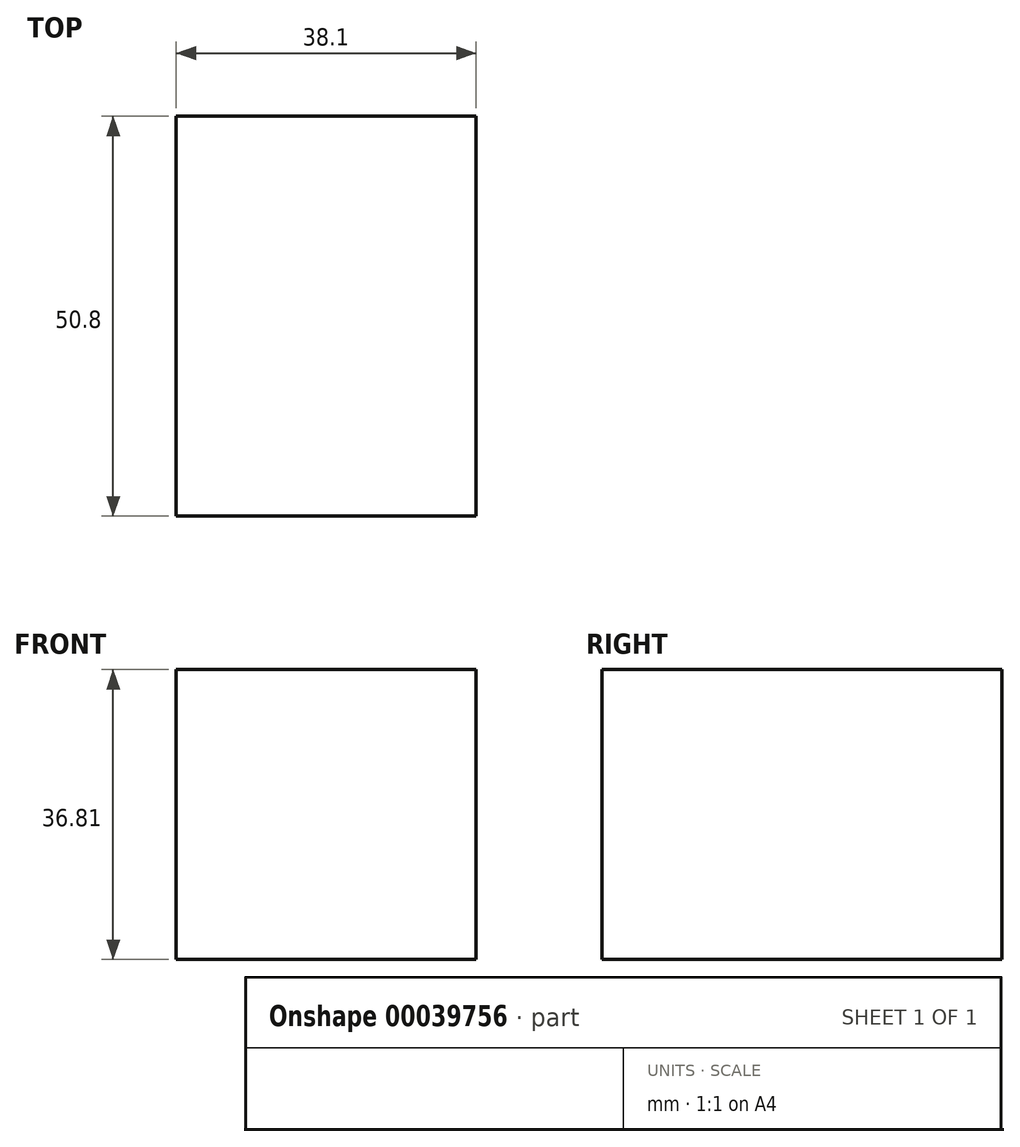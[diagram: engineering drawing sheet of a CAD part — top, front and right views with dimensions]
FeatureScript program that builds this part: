
annotation { "Feature Type Name" : "Feature", "Feature Type Description" : "" }
export const myFeature = defineFeature(function(context is Context, id is Id, definition is map)
    precondition{}
    {
        {
            var Q0;
            Q0=qCreatedBy(makeId("Front.planeOp"),FACE);
            var sketch = newSketch(context, id + "F0", { "sketchPlane" : qUnion([Q0])});
            skLineSegment(sketch, "E0.bottom", {"start": v(0, 0) * mm, "end": v(38.1, 0) * mm});
            skLineSegment(sketch, "E0.top", {"start": v(0, 36.8) * mm, "end": v(38.1, 36.8) * mm});
            skLineSegment(sketch, "E0.left", {"start": v(0, 0) * mm, "end": v(0, 36.8) * mm});
            skLineSegment(sketch, "E0.right", {"start": v(38.1, 0) * mm, "end": v(38.1, 36.8) * mm});
            skSolve(sketch);
        }
        {
            var Q0;
            Q0 = qSketchRegion(id + "F0", true);
            extrude(context, id + "F1", {"entities" : qUnion([Q0]), "depth" : 50.8 * mm});
        }
    });
